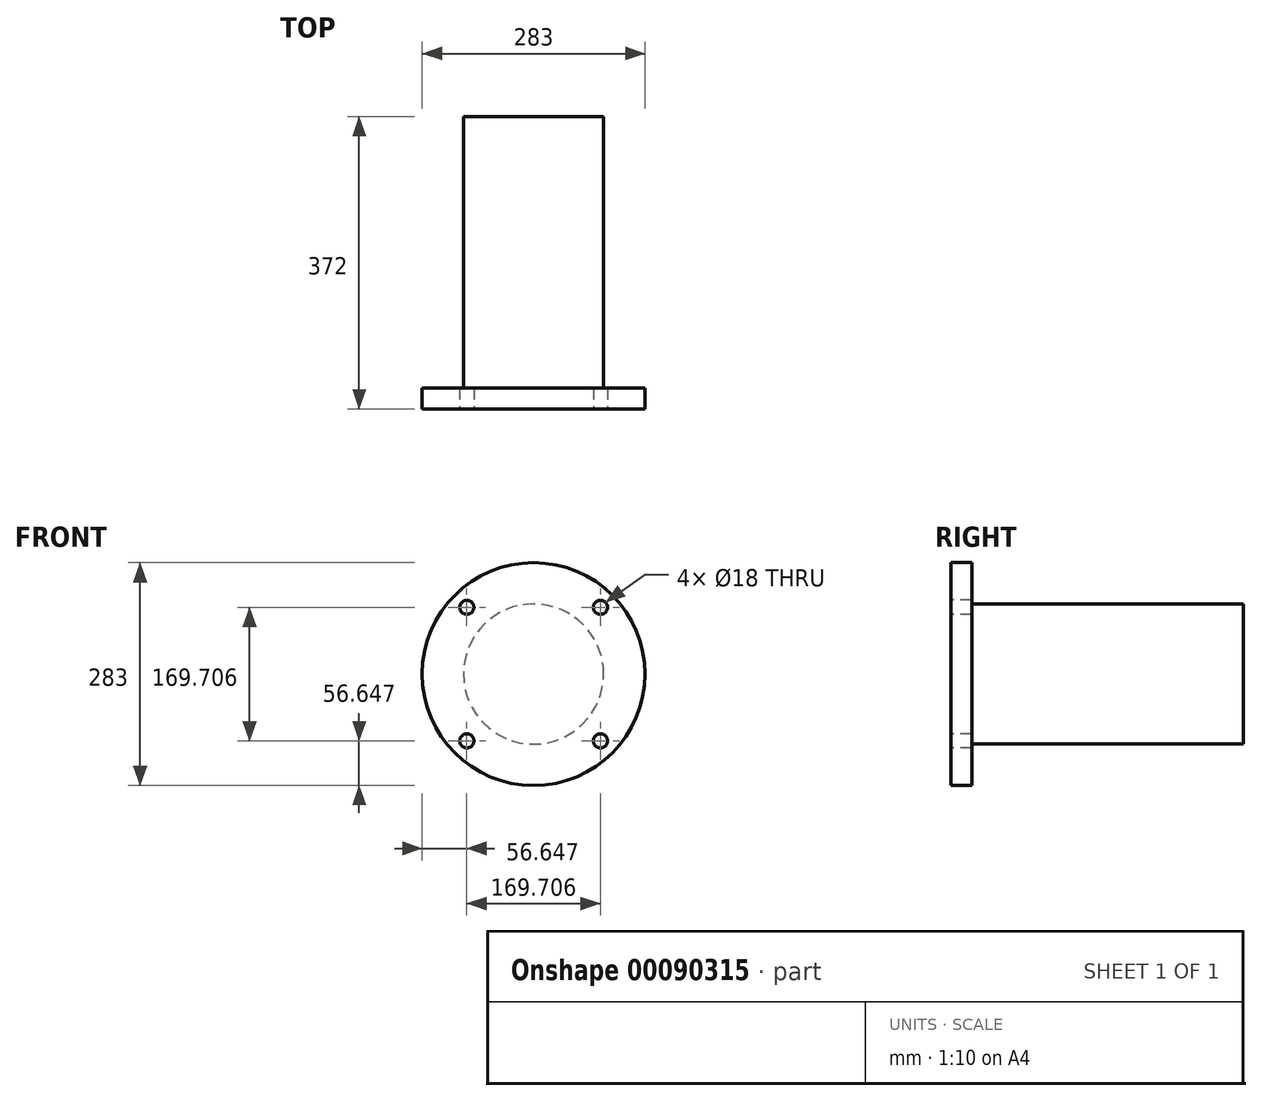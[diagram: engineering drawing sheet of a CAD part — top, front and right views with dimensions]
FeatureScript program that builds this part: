
annotation { "Feature Type Name" : "Feature", "Feature Type Description" : "" }
export const myFeature = defineFeature(function(context is Context, id is Id, definition is map)
    precondition{}
    {
        {
            var Q0;
            Q0=qCreatedBy(makeId("Front.planeOp"),FACE);
            var sketch = newSketch(context, id + "F0", { "sketchPlane" : qUnion([Q0])});
            skCircle(sketch, "E0", {"center": v(0, 0) * mm, "radius": 89 * mm});
            skSolve(sketch);
        }
        {
            var Q0;
            Q0 = qSketchRegion(id + "F0", true);
            extrude(context, id + "F1", {"entities" : qUnion([Q0]), "depth" : 345 * mm});
        }
        {
            var Q0;
            Q0=makeQuery(id+"F1.opExtrude","CAP_FACE",FACE,{"disambiguationData":[OSD([sQuery(id+"F0.wireOp",EDGE,"E0")])],"isStart":false});
            var sketch = newSketch(context, id + "F2", { "sketchPlane" : qUnion([Q0])});
            skCircle(sketch, "E1", {"center": v(0, 0) * mm, "radius": 141.5 * mm});
            skSolve(sketch);
        }
        {
            var Q0;
            Q0 = qSketchRegion(id + "F2", true);
            extrude(context, id + "F3", {"entities" : qUnion([Q0]), "operationType" : NewBodyOperationType.ADD, "depth" : 27 * mm});
        }
        {
            var Q0;
            Q0=makeQuery(id+"F3.opExtrude","CAP_FACE",FACE,{"disambiguationData":[OSD([sQuery(id+"F2.wireOp",EDGE,"E1")])],"isStart":false});
            var sketch = newSketch(context, id + "F4", { "sketchPlane" : qUnion([Q0])});
            skCircle(sketch, "E2", {"center": v(0, 0) * mm, "radius": 120 * mm, "construction": true});
            skLineSegment(sketch, "E3", {"start": v(0, 0) * mm, "end": v(0, 338.61) * mm, "construction": true});
            skCircle(sketch, "E4", {"center": v(-84.85, 84.85) * mm, "radius": 9 * mm});
            skLineSegment(sketch, "E5", {"start": v(0, 0) * mm, "end": v(-84.85, 84.85) * mm, "construction": true});
            skCircle(sketch, "E6.1.0", {"center": v(-84.85, -84.85) * mm, "radius": 9 * mm});
            skCircle(sketch, "E6.2.0", {"center": v(84.85, -84.85) * mm, "radius": 9 * mm});
            skCircle(sketch, "E6.3.0", {"center": v(84.85, 84.85) * mm, "radius": 9 * mm});
            skSolve(sketch);
        }
        {
            var Q0;
            Q0 = qSketchRegion(id + "F4", true);
            extrude(context, id + "F5", {"entities" : qUnion([Q0]), "operationType" : NewBodyOperationType.REMOVE, "endBound" : BoundingType.THROUGH_ALL, "oppositeDirection" : true, "depth" : 25 * mm});
        }
    });
